# Revit family: GVI_TR
name_source: partatom
category: Generic Models
units: mm (PartAtom-declared; Revit-internal decimal feet)

## family parameters
Can host rebar = No
Cut with Voids When Loaded = No
Maintain Annotation Orientation = No
Part Type = Normal
Room Calculation Point = No
Round Connector Dimension = Use Diameter
Shared = No

## types (6) — shared parameters
Description = Zelfdragende goot
Manufacturer = Meilof Riks B.V.
URL = https://www.meilofriks.nl
zero-valued in all types: Default Elevation

## per-type parameters (varying)
| type | Achterzijde_hoogte | Diepte | Diepte_bak | Voorzijde_hoogte |
| GVI S500B | 226 mm  [stored 0.74147 ft] | 500 mm  [stored 1.64042 ft] | 79 mm | 213 mm  [stored 0.698819 ft] |
| GVI S450B | 251 mm | 450 mm  [stored 1.47638 ft] | 104 mm | 238 mm |
| GVI S400B | 227 mm | 400 mm  [stored 1.31234 ft] | 78 mm | 212 mm |
| GVI S365B | 243 mm | 365 mm | 97 mm | 231 mm |
| GVI S310B | 219 mm | 310 mm | 76 mm  [stored 0.249344 ft] | 210 mm |
| GVI S280B | 210 mm | 280 mm | 91 mm | 199 mm |

note: column(s) folded — value = type name in every type: Model

note: [stored X ft] marks values corroborated as IEEE doubles in the binary element streams (Revit-internal decimal feet)

## geometry (parser evidence)
native form markers: Sweep x9
no freeform markers — native parametric forms only
